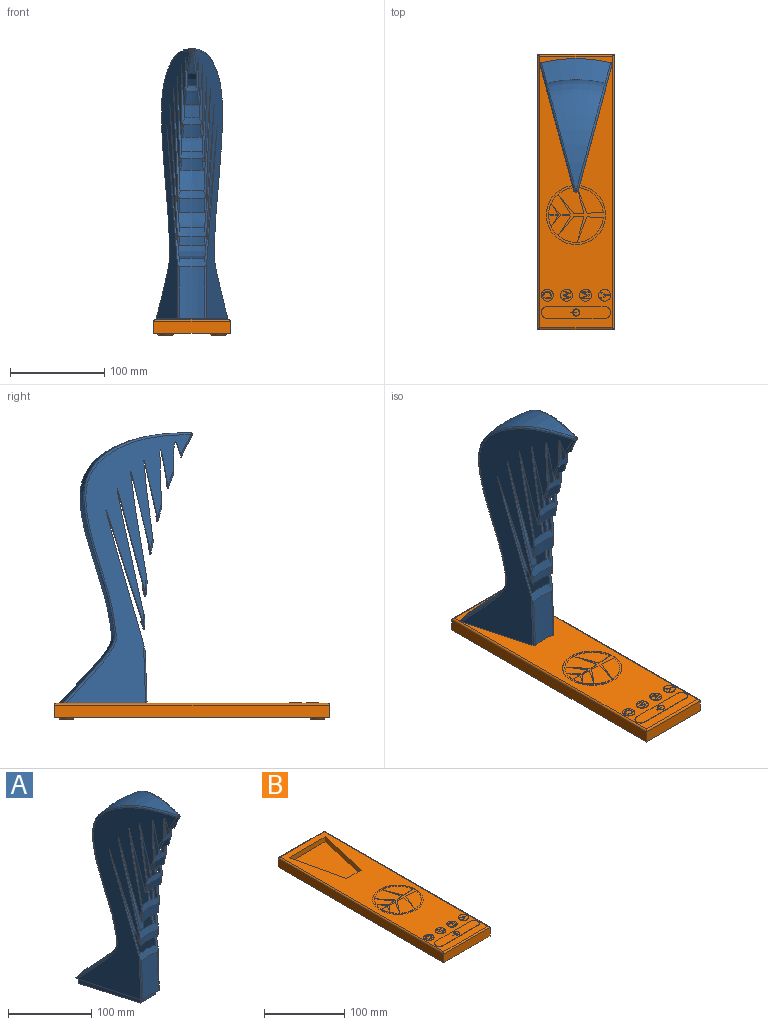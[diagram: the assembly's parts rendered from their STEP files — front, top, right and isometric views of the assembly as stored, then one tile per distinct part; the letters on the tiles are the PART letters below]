
ASSEMBLY  parts=2 mates=1
PART A: 52 faces, bbox 87x152.1x303.9 mm
  f0: revolved ~23.64x12.12mm, area 287mm2, adj f1,f14,f40,f46
  f1: revolved ~117.53x39.26mm, area 1388.8mm2, adj f0,f2,f15,f16,f17,f18,f26,f27
  f2: revolved ~26.47x14.93mm, area 395.3mm2, adj f1,f3,f39,f45
  f3: revolved ~139.89x46.83mm, area 1843.3mm2, adj f2,f4,f15,f16,f18,f19,f26,f27
  f4: revolved ~27.13x9.06mm, area 247.8mm2, adj f3,f5,f38,f44
  f5: revolved ~149.06x53.18mm, area 1937.6mm2, adj f4,f6,f15,f16,f19,f20,f26,f27
  f6: revolved ~55.87x26.96mm, area 1486.5mm2, adj f5,f7,f37,f43
  f7: plane 94.85x77.08mm, normal (0,0,-1), area 974mm2, adj f6,f8,f15,f16,f28,f31,f37,f43
  f8: revolved ~287.56x140.73mm, area 19235.2mm2, adj f7,f28,f31,f34
  f9: revolved ~23x12.24mm, area 96mm2, adj f10,f29,f30,f34
  f10: revolved ~35.71x14.74mm, area 344.5mm2, adj f9,f11,f15,f16,f23,f24,f26,f27
  f11: revolved ~14.28x13.96mm, area 193.5mm2, adj f10,f12,f36,f42
  f12: revolved ~62.81x22.54mm, area 699.2mm2, adj f11,f13,f15,f16,f24,f25,f26,f27
  f13: revolved ~19.69x13.48mm, area 264.4mm2, adj f12,f14,f35,f41
  f14: revolved ~87.58x31.64mm, area 1021mm2, adj f0,f13,f15,f16,f17,f25,f26,f27
  f15: plane 285.6x133.24mm, normal (0.97,-0.26,0), area 14586.4mm2, adj f1,f3,f5,f7,f10,f12,f14,f28
  f16: plane 285.6x133.24mm, normal (-0.97,-0.26,0), area 14586.4mm2, adj f1,f3,f5,f7,f10,f12,f14,f30
  f17: revolved ~23.21x13.4mm, area 310.4mm2, adj f1,f14,f26,f27
  f18: revolved ~26.31x16.49mm, area 432.6mm2, adj f1,f3,f26,f27
  f19: revolved ~27.22x11.49mm, area 314.7mm2, adj f3,f5,f26,f27
  f20: revolved ~62.58x27.21mm, area 1680.2mm2, adj f5,f21,f26,f27
  f21: plane 85.52x69.53mm, normal (0,0,1), area 4053.7mm2, adj f20,f22,f26,f27
  f22: revolved ~282.48x133.85mm, area 17907.6mm2, adj f21,f23,f26,f27
  f23: revolved ~19.93x10.67mm, area 69.7mm2, adj f10,f22,f26,f27
  f24: revolved ~15.81x13.15mm, area 196.7mm2, adj f10,f12,f26,f27
  f25: revolved ~19.07x15.35mm, area 288.8mm2, adj f12,f14,f26,f27
  f26: plane 290.75x137.56mm, normal (-0.97,0.26,0), area 14707.2mm2, adj f1,f3,f5,f10,f12,f14,f17,f18
  f27: plane 290.75x137.56mm, normal (0.97,0.26,0), area 14707.2mm2, adj f1,f3,f5,f10,f12,f14,f17,f18
  f28: bspline ~291.39x140.37mm, area 1251mm2, adj f7,f8,f15,f32
  f29: bspline ~31.64x17.08mm, area 72.8mm2, adj f9,f10,f15,f32
  f30: bspline ~31.64x17.08mm, area 72.8mm2, adj f9,f10,f16,f33
  f31: bspline ~291.39x140.37mm, area 1251mm2, adj f7,f8,f16,f33
  f32: sphere r=2mm, area 7.1mm2, adj f28,f29,f34
  f33: sphere r=2mm, area 7.1mm2, adj f30,f31,f34
  f34: torus R=9.34mm, axis (0,0,-1), area 3.1mm2, adj f8,f9,f32,f33
  f35: bspline ~61.36x17.05mm, area 45.2mm2, adj f12,f13,f14,f16
  f36: bspline ~51.69x21.02mm, area 48.4mm2, adj f10,f11,f12,f16
  f37: bspline ~72.64x4.24mm, area 183.1mm2, adj f5,f6,f7,f16
  f38: bspline ~35.95x2.53mm, area 30.8mm2, adj f3,f4,f5,f16
  f39: bspline ~47.82x6.72mm, area 48mm2, adj f1,f2,f3,f16
  f40: bspline ~51.24x11.38mm, area 39.5mm2, adj f0,f1,f14,f16
  f41: bspline ~80.43x23.82mm, area 45.2mm2, adj f12,f13,f14,f15
  f42: bspline ~51.69x21.02mm, area 48.4mm2, adj f10,f11,f12,f15
  f43: bspline ~72.64x4.24mm, area 183.1mm2, adj f5,f6,f7,f15
  f44: bspline ~35.95x2.53mm, area 30.8mm2, adj f3,f4,f5,f15
  f45: bspline ~47.82x6.72mm, area 48mm2, adj f1,f2,f3,f15
  f46: bspline ~51.24x11.38mm, area 39.5mm2, adj f0,f1,f14,f15
  f47: plane 81.21x23.89mm, normal (-0.96,-0.28,0), area 634.9mm2, adj f7,f48,f50,f51
  f48: plane 73.63x7.5mm, normal (0,1,0), area 552.2mm2, adj f7,f47,f49,f51
  f49: plane 81.21x23.89mm, normal (0.96,-0.28,0), area 634.9mm2, adj f7,f48,f50,f51
  f50: plane 25.86x7.5mm, normal (0,-1,0), area 194mm2, adj f7,f47,f49,f51
  f51: plane 81.21x73.63mm, normal (0,0,-1), area 4039.8mm2, adj f47,f48,f49,f50
PART B: 136 faces, bbox 81.3x292.1x17.5 mm
  f0: plane 73.66x12.7mm, normal (0,0,1), area 883mm2, adj f20,f21,f22,f23,f90,f91,f92,f93
  f1: plane 12.7x12.7mm, normal (0,0,1), area 109.6mm2, adj f19,f80,f81,f82,f83,f84,f85,f86
  f2: plane 12.7x12.7mm, normal (0,0,1), area 99.3mm2, adj f18,f61,f62,f63,f64,f65,f66,f67
  f3: plane 12.7x12.7mm, normal (0,0,1), area 103.5mm2, adj f17,f40,f41,f42,f43,f44,f45,f46
  f4: plane 12.7x12.7mm, normal (0,0,1), area 71.7mm2, adj f16,f24,f25,f26,f27,f28,f29,f37
  f5: plane 288.1x77.28mm, normal (0,0,1), area 14065.7mm2, adj f11,f12,f13,f14,f16,f17,f18,f19
  f6: plane 81.28x13mm, normal (0,-1,0), area 1056.6mm2, adj f7,f9,f10,f124
  f7: plane 292.1x81.28mm, normal (0,0,-1), area 22601.8mm2, adj f6,f8,f9,f10,f132,f133,f134,f135
  f8: plane 81.28x13mm, normal (0,1,0), area 1056.6mm2, adj f7,f9,f10,f127
  f9: plane 292.1x13mm, normal (1,0,0), area 3797.3mm2, adj f6,f7,f8,f125
  f10: plane 292.1x13mm, normal (-1,0,0), area 3797.3mm2, adj f6,f7,f8,f126
  f11: plane 25.91x7.5mm, normal (0,1,0), area 194.3mm2, adj f5,f12,f14,f15
  f12: plane 82.56x18.75mm, normal (-0.98,0.22,0), area 634.9mm2, adj f5,f11,f13,f15
  f13: plane 63.4x7.5mm, normal (0,-1,0), area 475.5mm2, adj f5,f12,f14,f15
  f14: plane 82.56x18.75mm, normal (0.98,0.22,0), area 634.9mm2, adj f5,f11,f13,f15
  f15: plane 82.56x63.4mm, normal (0,0,1), area 3686.4mm2, adj f11,f12,f13,f14
  f16: cylinder r=6.35mm len=12.7mm, axis (0,0,-1), area 19.9mm2, adj f4,f5
  f17: cylinder r=6.35mm len=12.7mm, axis (0,0,-1), area 19.9mm2, adj f3,f5
  f18: cylinder r=6.35mm len=12.7mm, axis (0,0,-1), area 19.9mm2, adj f2,f5
  f19: cylinder r=6.35mm len=12.7mm, axis (0,0,-1), area 19.9mm2, adj f1,f5
  f20: cylinder r=6.35mm len=12.7mm, axis (0,0,-1), area 10.3mm2, adj f0,f5,f21,f23
  f21: plane 60.83x0.5mm, normal (0,-1,0), area 30.4mm2, adj f0,f5,f20,f22
  f22: cylinder r=6.35mm len=12.68mm, axis (0,0,-1), area 9.6mm2, adj f0,f5,f21,f23
  f23: plane 61.21x0.5mm, normal (0,1,0), area 30.6mm2, adj f0,f5,f20,f22
  f24: extruded ~3.18x1.14mm, area 1.7mm2, adj f4,f25,f37,f38
  f25: extruded ~3.2x1.14mm, area 1.7mm2, adj f4,f24,f26,f38
  f26: plane 2.7x0.5mm, normal (1,0,0), area 1.4mm2, adj f4,f25,f27,f38
  f27: plane 8.81x0.5mm, normal (0,1,0), area 4.4mm2, adj f4,f26,f28,f38
  f28: plane 2.44x0.5mm, normal (-1,0,0), area 1.2mm2, adj f4,f27,f29,f38
  f29: extruded ~3.41x1.15mm, area 1.8mm2, adj f4,f28,f37,f38
  f30: extruded ~2.67x0.92mm, area 1.4mm2, adj f31,f36,f38,f39
  f31: extruded ~2.76x0.9mm, area 1.5mm2, adj f30,f32,f38,f39
  f32: plane 1.25x0.5mm, normal (1,0,0), area 0.6mm2, adj f31,f33,f38,f39
  f33: plane 7.04x0.5mm, normal (0,-1,0), area 3.5mm2, adj f32,f34,f38,f39
  f34: plane 1.49x0.5mm, normal (-1,0,0), area 0.7mm2, adj f33,f35,f38,f39
  f35: extruded ~2.57x0.87mm, area 1.4mm2, adj f34,f36,f38,f39
  f36: extruded ~2.6x0.87mm, area 1.4mm2, adj f30,f35,f38,f39
  f37: extruded ~3.34x1.18mm, area 1.8mm2, adj f4,f24,f29,f38
  f38: plane 8.81x7.03mm, normal (0,0,1), area 24.6mm2, adj f24,f25,f26,f27,f28,f29,f30,f31
  f39: plane 7.04x4.93mm, normal (0,0,1), area 30.5mm2, adj f30,f31,f32,f33,f34,f35,f36
  f40: plane 7.38x1.97mm, normal (-0.26,-0.97,0), area 3.8mm2, adj f3,f41,f59,f60
  f41: plane 0.91x0.5mm, normal (1,0,0), area 0.5mm2, adj f3,f40,f42,f60
  f42: plane 4.55x1.16mm, normal (0.25,0.97,0), area 2.3mm2, adj f3,f41,f43,f60
  f43: extruded ~1.75x0.5mm, area 0.9mm2, adj f3,f42,f44,f60
  f44: extruded ~1.77x0.5mm, area 0.9mm2, adj f3,f43,f45,f60
  f45: plane 4.53x1.39mm, normal (0.29,-0.96,0), area 2.4mm2, adj f3,f44,f46,f60
  f46: plane 0.91x0.5mm, normal (1,0,0), area 0.5mm2, adj f3,f45,f47,f60
  f47: plane 4.49x1.32mm, normal (0.28,0.96,0), area 2.3mm2, adj f3,f46,f48,f60
  f48: extruded ~1.81x0.5mm, area 0.9mm2, adj f3,f47,f49,f60
  f49: extruded ~1.74x0.5mm, area 0.9mm2, adj f3,f48,f50,f60
  f50: plane 4.56x1.17mm, normal (0.25,-0.97,0), area 2.4mm2, adj f3,f49,f51,f60
  f51: plane 0.91x0.5mm, normal (1,0,0), area 0.5mm2, adj f3,f50,f52,f60
  f52: plane 7.38x1.96mm, normal (-0.26,0.97,0), area 3.8mm2, adj f3,f51,f53,f60
  f53: plane 0.85x0.5mm, normal (-1,0,0), area 0.4mm2, adj f3,f52,f54,f60
  f54: plane 4.91x1.44mm, normal (-0.28,-0.96,0), area 2.6mm2, adj f3,f53,f55,f60
  f55: extruded ~1.46x0.5mm, area 0.8mm2, adj f3,f54,f56,f60
  f56: extruded ~0.6x0.5mm, area 0.3mm2, adj f3,f55,f57,f60
  f57: extruded ~0.83x0.5mm, area 0.4mm2, adj f3,f56,f58,f60
  f58: plane 4.94x1.49mm, normal (-0.29,0.96,0), area 2.6mm2, adj f3,f57,f59,f60
  f59: plane 0.85x0.5mm, normal (-1,0,0), area 0.4mm2, adj f3,f40,f58,f60
  f60: plane 9.29x7.38mm, normal (0,0,1), area 23.2mm2, adj f40,f41,f42,f43,f44,f45,f46,f47
  f61: plane 0.75x0.5mm, normal (-1,0,0), area 0.4mm2, adj f2,f62,f78,f79
  f62: plane 7.08x2.74mm, normal (-0.36,-0.93,0), area 3.8mm2, adj f2,f61,f63,f79
  f63: plane 0.5x0.04mm, normal (-1,0,0), area 0mm2, adj f2,f62,f64,f79
  f64: extruded ~1.93x0.5mm, area 1mm2, adj f2,f63,f65,f79
  f65: plane 5.15x0.5mm, normal (0,1,0), area 2.6mm2, adj f2,f64,f66,f79
  f66: plane 0.93x0.5mm, normal (-1,0,0), area 0.5mm2, adj f2,f65,f67,f79
  f67: plane 8x0.5mm, normal (0,-1,0), area 4mm2, adj f2,f66,f68,f79
  f68: plane 1.39x0.5mm, normal (1,0,0), area 0.7mm2, adj f2,f67,f69,f79
  f69: plane 6.6x2.55mm, normal (0.36,0.93,0), area 3.5mm2, adj f2,f68,f70,f79
  f70: plane 0.5x0.04mm, normal (1,0,0), area 0mm2, adj f2,f69,f71,f79
  f71: plane 6.6x2.53mm, normal (0.36,-0.93,0), area 3.5mm2, adj f2,f70,f72,f79
  f72: plane 1.4x0.5mm, normal (1,0,0), area 0.7mm2, adj f2,f71,f73,f79
  f73: plane 8x0.5mm, normal (0,1,0), area 4mm2, adj f2,f72,f74,f79
  f74: plane 0.86x0.5mm, normal (-1,0,0), area 0.4mm2, adj f2,f73,f75,f79
  f75: plane 5.09x0.5mm, normal (0,-1,0), area 2.5mm2, adj f2,f74,f76,f79
  f76: extruded ~2x0.5mm, area 1mm2, adj f2,f75,f77,f79
  f77: plane 0.5x0.04mm, normal (-1,0,0), area 0mm2, adj f2,f76,f78,f79
  f78: plane 7.09x2.71mm, normal (-0.36,0.93,0), area 3.8mm2, adj f2,f61,f77,f79
  f79: plane 8x7.92mm, normal (0,0,1), area 27.3mm2, adj f61,f62,f63,f64,f65,f66,f67,f68
  f80: plane 4.75x2.51mm, normal (0.47,-0.88,0), area 2.7mm2, adj f1,f81,f88,f89
  f81: plane 1.21x0.5mm, normal (1,0,0), area 0.6mm2, adj f1,f80,f82,f89
  f82: plane 5.86x3.16mm, normal (-0.47,0.88,0), area 3.3mm2, adj f1,f81,f83,f89
  f83: plane 3.63x0.5mm, normal (0,1,0), area 1.8mm2, adj f1,f82,f84,f89
  f84: plane 1.12x0.5mm, normal (-1,0,0), area 0.6mm2, adj f1,f83,f85,f89
  f85: plane 3.68x0.5mm, normal (0,-1,0), area 1.8mm2, adj f1,f84,f86,f89
  f86: plane 5.81x3.17mm, normal (-0.48,-0.88,0), area 3.3mm2, adj f1,f85,f87,f89
  f87: plane 1.19x0.5mm, normal (1,0,0), area 0.6mm2, adj f1,f86,f88,f89
  f88: plane 4.75x2.53mm, normal (0.47,0.88,0), area 2.7mm2, adj f1,f80,f87,f89
  f89: plane 9.49x7.45mm, normal (0,0,1), area 17.1mm2, adj f80,f81,f82,f83,f84,f85,f86,f87
  f90: cylinder r=3.24mm len=6.48mm, axis (0,0,1), area 9mm2, adj f0,f91,f93,f94
  f91: plane 0.53x0.5mm, normal (0.38,-0.93,0), area 0.3mm2, adj f0,f90,f92,f94
  f92: cylinder r=3.81mm len=7.62mm, axis (0,0,1), area 10.6mm2, adj f0,f91,f93,f94
  f93: plane 0.53x0.5mm, normal (0.34,0.94,0), area 0.3mm2, adj f0,f90,f92,f94
  f94: plane 7.62x7.39mm, normal (0,0,1), area 11.1mm2, adj f90,f91,f92,f93
  f95: plane 6.6x0.5mm, normal (0,1,0), area 3.3mm2, adj f0,f96,f98,f99
  f96: plane 0.81x0.5mm, normal (-1,0,0), area 0.4mm2, adj f0,f95,f97,f99
  f97: plane 6.6x0.5mm, normal (0,-1,0), area 3.3mm2, adj f0,f96,f98,f99
  f98: plane 0.81x0.5mm, normal (1,0,0), area 0.4mm2, adj f0,f95,f97,f99
  f99: plane 6.6x0.81mm, normal (0,0,1), area 5.4mm2, adj f95,f96,f97,f98
  f100: plane 10.48x9.54mm, normal (-0.74,0.67,0), area 7.1mm2, adj f101,f120,f122,f123
  f101: plane 10.13x0.5mm, normal (0.05,1,0), area 5.1mm2, adj f100,f102,f122,f123
  f102: plane 19.97x12.34mm, normal (0.85,-0.53,0), area 11.7mm2, adj f101,f103,f122,f123
  f103: plane 19.79x15.88mm, normal (-0.78,0.63,0), area 12.7mm2, adj f102,f104,f122,f123
  f104: plane 10.63x0.52mm, normal (0.05,1,0), area 5.3mm2, adj f103,f105,f122,f123
  f105: plane 25.98x6.66mm, normal (0.97,-0.25,0), area 13.4mm2, adj f104,f106,f122,f123
  f106: plane 25.81x10.11mm, normal (-0.93,0.36,0), area 13.9mm2, adj f105,f107,f122,f123
  f107: plane 17.11x1.05mm, normal (0.06,1,0), area 8.6mm2, adj f106,f108,f122,f123
  f108: cylinder r=29.06mm len=58.13mm, axis (0,0,1), area 88.4mm2, adj f107,f109,f122,f123
  f109: plane 17.13x0.84mm, normal (0.05,-1,0), area 8.6mm2, adj f108,f110,f122,f123
  f110: plane 25.81x10.11mm, normal (-0.93,-0.36,0), area 13.9mm2, adj f109,f111,f122,f123
  f111: plane 25.98x6.66mm, normal (0.97,0.25,0), area 13.4mm2, adj f110,f112,f122,f123
  f112: plane 10.63x0.52mm, normal (0.05,-1,0), area 5.3mm2, adj f111,f113,f122,f123
  f113: plane 19.79x15.88mm, normal (-0.78,-0.63,0), area 12.7mm2, adj f112,f114,f122,f123
  f114: plane 19.97x12.34mm, normal (0.85,0.53,0), area 11.7mm2, adj f113,f115,f122,f123
  f115: plane 10.13x0.5mm, normal (0.05,-1,0), area 5.1mm2, adj f114,f116,f122,f123
  f116: plane 10.48x9.54mm, normal (-0.74,-0.67,0), area 7.1mm2, adj f115,f117,f122,f123
  f117: plane 10.63x6.57mm, normal (0.85,0.53,0), area 6.2mm2, adj f116,f118,f122,f123
  f118: plane 8.86x0.5mm, normal (0.05,-1,0), area 4.4mm2, adj f117,f119,f122,f123
  f119: plane 8.86x0.5mm, normal (0.05,1,0), area 4.4mm2, adj f118,f120,f122,f123
  f120: plane 10.63x6.57mm, normal (0.85,-0.53,0), area 6.2mm2, adj f100,f119,f122,f123
  f121: cylinder r=31.44mm len=62.89mm, axis (0,0,1), area 98.8mm2, adj f5,f122
  f122: plane 62.89x62.89mm, normal (0,0,1), area 809.4mm2, adj f100,f101,f102,f103,f104,f105,f106,f107
  f123: plane 58.13x57.99mm, normal (0,0,1), area 2296.7mm2, adj f100,f101,f102,f103,f104,f105,f106,f107
  f124: cylinder r=2mm len=81.28mm, axis (1,0,0), area 250.8mm2, adj f5,f6,f125,f126
  f125: cylinder r=2mm len=292.1mm, axis (0,1,0), area 913.1mm2, adj f5,f9,f124,f127
  f126: cylinder r=2mm len=292.1mm, axis (0,-1,0), area 913.1mm2, adj f5,f10,f124,f127
  f127: cylinder r=2mm len=81.28mm, axis (-1,0,0), area 250.8mm2, adj f5,f8,f125,f126
  f128: plane 15.05x15.05mm, normal (0,0,-1), area 177.9mm2, adj f135
  f129: plane 15.05x15.05mm, normal (0,0,-1), area 177.9mm2, adj f134
  f130: plane 15.05x15.05mm, normal (0,0,-1), area 177.9mm2, adj f133
  f131: plane 15.05x15.05mm, normal (0,0,-1), area 177.9mm2, adj f132
  f132: cone r=7.52mm half-angle=45deg, axis (0,0,1), area 151.5mm2, adj f7,f131
  f133: cone r=7.52mm half-angle=45deg, axis (0,0,1), area 151.5mm2, adj f7,f130
  f134: cone r=7.52mm half-angle=45deg, axis (0,0,1), area 151.5mm2, adj f7,f129
  f135: cone r=7.52mm half-angle=45deg, axis (0,0,1), area 151.5mm2, adj f7,f128
PLACE A t=(-152.8,-8.62,79.74)mm
PLACE B t=(-193.44,-79.84,-82.67)mm
MATE parallel B.f15 <-> A.f51  axis (0,0,1) through (-152.8,14.93,-86.31)mm
